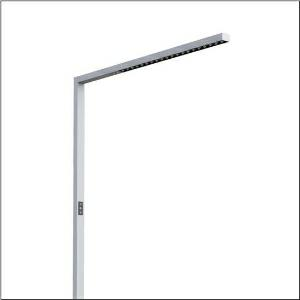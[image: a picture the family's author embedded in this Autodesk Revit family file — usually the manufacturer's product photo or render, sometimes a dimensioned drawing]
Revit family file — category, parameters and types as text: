
# Revit family: silica_31_floor_51my52fatcs
name_source: partatom
category: Lighting Fixtures
units: mm (PartAtom-declared; Revit-internal decimal feet)

## family parameters
Cut with Voids When Loaded = No
Host = Face
Light Source = No
Part Type = Normal
Room Calculation Point = No
Round Connector Dimension = Use Diameter
Shared = No

## types (1)
- --- (1 x LED, 8520 lm, 71 W, 4000K)
    Apparent Load = 71 VA
    CIE Flux Codes = 86 100 100 24 100
    Color Rendering = 80
    Color Temperature = 4000K
    Default Elevation = 1800 mm
    Description = Silica® 31 Floor, floorstanding luminaire, secondary optical cover: cover panel, of PMMA, light emission: direct/indirect distribution, primary light characteristic: symmetric, installation type: not mounted, LED, rated luminous flux: 8.520lm, luminous efficacy: 120lm/W, light colour: 8tw, colour temperature: 2700..6500K, control gear: Touchdim, daylight-dependent control, with cable with plug, mains connection: 230V, AC, 50Hz, connection cable included, cable length: 2,5m, rated input power: 71W, luminaire head, of aluminium, metallic grey (RAL 9006), length: 1.203mm, width: 52mm, supporting column, angular, of aluminium, metallic grey (RAL 9006), baseplate, of steel, metallic grey (RAL 9006), local control - self-sufficient standalone sensors, direct and indirect component separately switchable, protection rating (complete): IP20, insulation class (complete): insulation class I (protective earthing), certification: CE, ENEC, permissible operating ambient temperature: -20..+40°C, standard: EN 50419, packaging unit: 1 piece
    Height = 36 mm
    Lamp = 1 x LED
    Lamp Light Flux = 8520 lm
    Lamp Power = 71 W
    Lamp count = 1
    Length = 1203 mm
    Luminous efficacy = 120 lm/W
    Manufacturer = Siteco
    ModVariant = No
    Model = 51MY52FATCS
    Mounting Place = Floor
    Mounting Type = Freestanding
    Number of Poles = 1
    OnlyDefault = Yes
    Power Factor = 1
    Product Name = Silica 31 Floor
    Product group = floorstanding luminaire
    ProductGroupID = 1302
    Protection Class = Protection class I
    Protection Degree = IP 20
    RLX_Detail_Level = 1
    RLX_Emergency_Light_Flux = 0 lm
    RLX_Emergency_Type = 0
    RLX_Emergency_Type_DB = No
    RlxData = <blob elided: 19757 chars, md5=770c79fd>
    Socket = socket
    Standby Power = 0 W
    System Light Flux = 8520 lm
    System Power = 71 W
    Type Comments = factory setting
    Type Image = l_1275303.jpg
    URL = http://relux.com
    VarID = @adj_087105
    Voltage = 0 V
    Weight = 0.00 kg
    Width = 52 mm  [stored 0.170604 ft]

note: [stored X ft] marks values corroborated as IEEE doubles in the binary element streams (Revit-internal decimal feet)

## geometry (parser evidence)
native form markers: Blend x4, Sweep x16
no freeform markers — native parametric forms only
